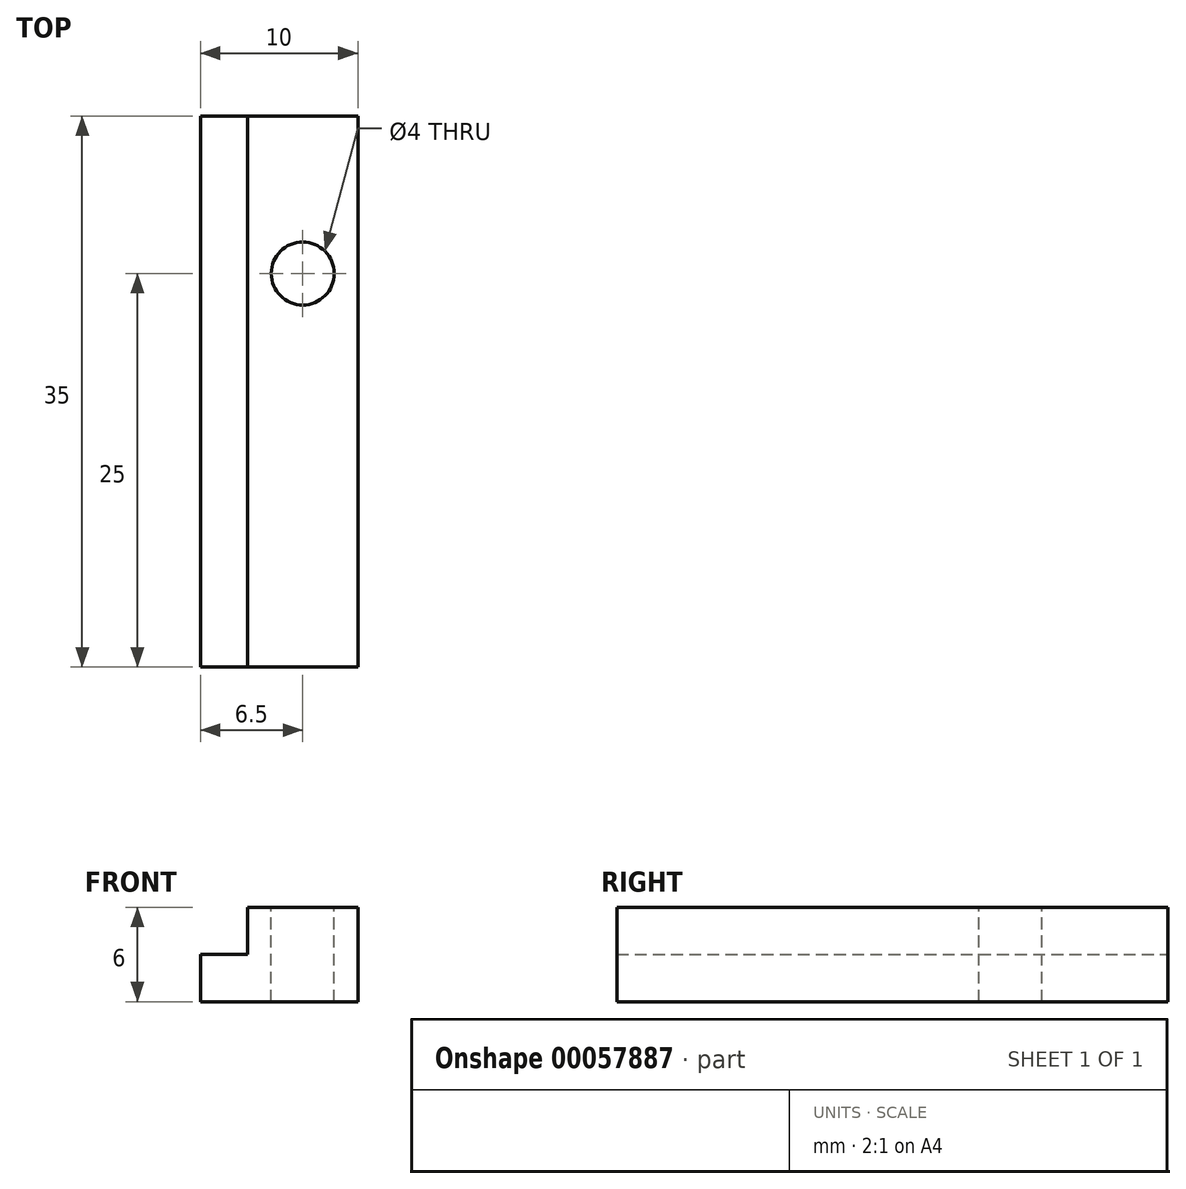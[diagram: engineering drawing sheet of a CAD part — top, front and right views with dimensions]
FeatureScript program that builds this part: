
annotation { "Feature Type Name" : "Feature", "Feature Type Description" : "" }
export const myFeature = defineFeature(function(context is Context, id is Id, definition is map)
    precondition{}
    {
        {
            var Q0;
            Q0=qCreatedBy(makeId("Top.planeOp"),FACE);
            var sketch = newSketch(context, id + "F0", { "sketchPlane" : qUnion([Q0])});
            skLineSegment(sketch, "E0.bottom", {"start": v(0, 0) * mm, "end": v(10, 0) * mm});
            skLineSegment(sketch, "E0.top", {"start": v(0, 35) * mm, "end": v(10, 35) * mm});
            skLineSegment(sketch, "E0.left", {"start": v(0, 0) * mm, "end": v(0, 35) * mm});
            skLineSegment(sketch, "E0.right", {"start": v(10, 0) * mm, "end": v(10, 35) * mm});
            skSolve(sketch);
        }
        {
            var Q0;
            Q0=qSketchRegion(id+"F0",true);
            extrude(context, id + "F1", {"entities" : qUnion([Q0]), "depth" : 6 * mm});
        }
        {
            var Q0;
            Q0=makeQuery(id+"F1.opExtrude","CAP_FACE",FACE,{"disambiguationData":[OSD([sQuery(id+"F0.wireOp",EDGE,"E0.bottom"),sQuery(id+"F0.wireOp",EDGE,"E0.top"),sQuery(id+"F0.wireOp",EDGE,"E0.left"),sQuery(id+"F0.wireOp",EDGE,"E0.right")])],"isStart":false});
            var sketch = newSketch(context, id + "F2", { "sketchPlane" : qUnion([Q0])});
            skLineSegment(sketch, "E1.bottom", {"start": v(0, 35) * mm, "end": v(3, 35) * mm});
            skLineSegment(sketch, "E1.top", {"start": v(0, 0) * mm, "end": v(3, 0) * mm});
            skLineSegment(sketch, "E1.left", {"start": v(0, 35) * mm, "end": v(0, 0) * mm});
            skLineSegment(sketch, "E1.right", {"start": v(3, 35) * mm, "end": v(3, 0) * mm});
            skSolve(sketch);
        }
        {
            var Q0;
            Q0=qSketchRegion(id+"F2",true);
            extrude(context, id + "F3", {"entities" : qUnion([Q0]), "operationType" : NewBodyOperationType.REMOVE, "oppositeDirection" : true, "depth" : 3 * mm});
        }
        {
            var Q0;
            Q0=makeQuery(id+"F1.opExtrude","CAP_FACE",FACE,{"disambiguationData":[OSD([sQuery(id+"F0.wireOp",EDGE,"E0.bottom"),sQuery(id+"F0.wireOp",EDGE,"E0.top"),sQuery(id+"F0.wireOp",EDGE,"E0.left"),sQuery(id+"F0.wireOp",EDGE,"E0.right")])],"isStart":false});
            var sketch = newSketch(context, id + "F4", { "sketchPlane" : qUnion([Q0])});
            skCircle(sketch, "E2", {"center": v(6.5, 25) * mm, "radius": 2 * mm});
            skPoint(sketch, "E3", {"position": v(6.5, 35) * mm});
            skLineSegment(sketch, "E4", {"start": v(6.5, 25) * mm, "end": v(6.5, 0) * mm});
            skSolve(sketch);
        }
        {
            var Q0;
            Q0=qSketchRegion(id+"F4",true);
            extrude(context, id + "F5", {"entities" : qUnion([Q0]), "operationType" : NewBodyOperationType.REMOVE, "oppositeDirection" : true, "depth" : 25 * mm});
        }
    });
